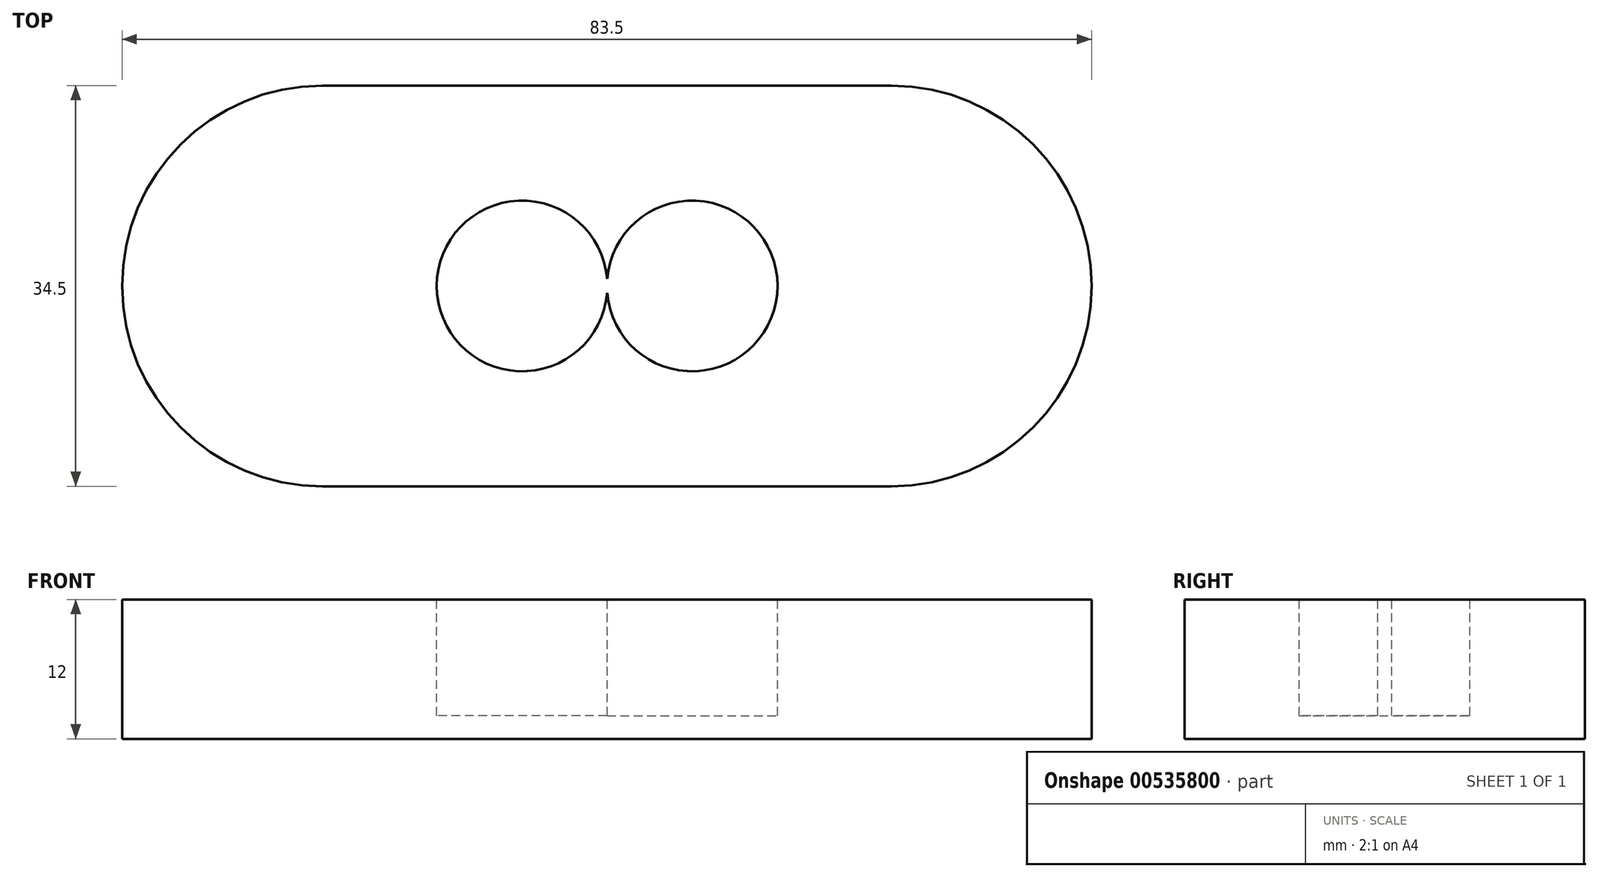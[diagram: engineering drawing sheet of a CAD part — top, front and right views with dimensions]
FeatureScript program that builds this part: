
annotation { "Feature Type Name" : "Feature", "Feature Type Description" : "" }
export const myFeature = defineFeature(function(context is Context, id is Id, definition is map)
    precondition{}
    {
        {
            var Q0;
            Q0=qCreatedBy(makeId("Top.planeOp"),FACE);
            var sketch = newSketch(context, id + "F0", { "sketchPlane" : qUnion([Q0])});
            skLineSegment(sketch, "E0.bottom", {"start": v(-24.5, 17.25) * mm, "end": v(24.5, 17.25) * mm});
            skLineSegment(sketch, "E0.top", {"start": v(-24.5, -17.25) * mm, "end": v(24.5, -17.25) * mm});
            skPoint(sketch, "E0.middle", {"position": v(0, 0) * mm});
            skArc(sketch, "E1", {"start": v(-24.5, 17.25) * mm, "mid": v(-41.75, 0) * mm, "end": v(-24.5, -17.25) * mm});
            skArc(sketch, "E2", {"start": v(24.5, -17.25) * mm, "mid": v(41.75, 0) * mm, "end": v(24.5, 17.25) * mm});
            skSolve(sketch);
        }
        {
            var Q0;
            Q0 = qSketchRegion(id + "F0", true);
            extrude(context, id + "F1", {"entities" : qUnion([Q0]), "depth" : 12 * mm, "offsetDistance" : 25 * mm});
        }
        {
            var Q0;
            Q0=makeQuery(id+"F1.opExtrude","CAP_FACE",FACE,{"disambiguationData":[OSD([sQuery(id+"F0.wireOp",EDGE,"E0.bottom"),sQuery(id+"F0.wireOp",EDGE,"E0.top"),sQuery(id+"F0.wireOp",EDGE,"E1"),sQuery(id+"F0.wireOp",EDGE,"E2")])],"isStart":false});
            var sketch = newSketch(context, id + "F2", { "sketchPlane" : qUnion([Q0])});
            skLineSegment(sketch, "E3", {"start": v(-41.75, 0) * mm, "end": v(41.75, 0) * mm, "construction": true});
            skArc(sketch, "E4", {"start": v(0.02, 0.6) * mm, "mid": v(-14.65, 0) * mm, "end": v(0.02, -0.6) * mm});
            skArc(sketch, "E5", {"start": v(0.02, -0.6) * mm, "mid": v(14.7, 0) * mm, "end": v(0.03, 0.6) * mm});
            skSolve(sketch);
        }
        {
            var Q0;
            Q0 = qSketchRegion(id + "F2", true);
            extrude(context, id + "F3", {"entities" : qUnion([Q0]), "operationType" : NewBodyOperationType.REMOVE, "oppositeDirection" : true, "depth" : 10 * mm, "offsetDistance" : 25 * mm});
        }
    });
